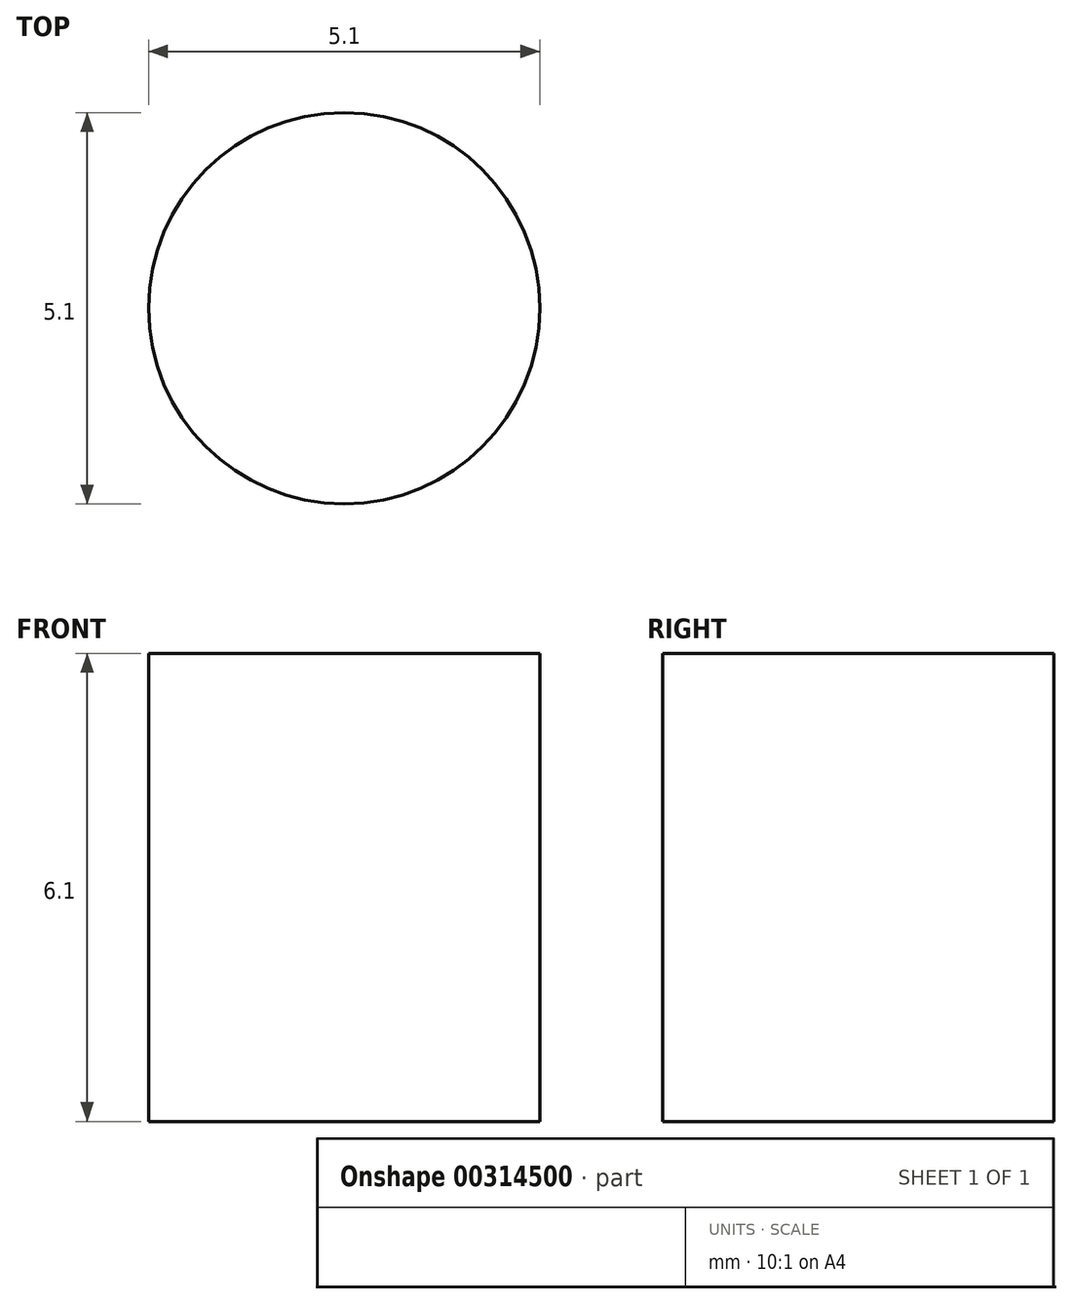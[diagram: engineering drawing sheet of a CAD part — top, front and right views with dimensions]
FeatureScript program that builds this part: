
annotation { "Feature Type Name" : "Feature", "Feature Type Description" : "" }
export const myFeature = defineFeature(function(context is Context, id is Id, definition is map)
    precondition{}
    {
        {
            var Q0;
            Q0=qCreatedBy(makeId("Top.planeOp"),FACE);
            var sketch = newSketch(context, id + "F0", { "sketchPlane" : qUnion([Q0])});
            skCircle(sketch, "E0", {"center": v(-26.5, 0) * mm, "radius": 2.55 * mm});
            skCircle(sketch, "E1", {"center": v(5.29, 10) * mm, "radius": 2.55 * mm});
            skCircle(sketch, "E2", {"center": v(5.29, 0) * mm, "radius": 2.55 * mm});
            skCircle(sketch, "E3", {"center": v(5.29, -10) * mm, "radius": 2.55 * mm});
            skCircle(sketch, "E4", {"center": v(25.29, -10) * mm, "radius": 2.55 * mm});
            skCircle(sketch, "E5", {"center": v(25.29, 0) * mm, "radius": 2.55 * mm});
            skCircle(sketch, "E6", {"center": v(25.29, 10) * mm, "radius": 2.55 * mm});
            skArc(sketch, "E7", {"start": v(-28.5, 19.75) * mm, "mid": v(-32.04, 18.29) * mm, "end": v(-33.5, 14.75) * mm});
            skLineSegment(sketch, "E8", {"start": v(-33.5, -14.75) * mm, "end": v(-33.5, 14.75) * mm});
            skArc(sketch, "E9", {"start": v(-33.5, -14.75) * mm, "mid": v(-32.04, -18.29) * mm, "end": v(-28.5, -19.75) * mm});
            skLineSegment(sketch, "E10", {"start": v(28.5, -19.75) * mm, "end": v(-28.5, -19.75) * mm});
            skArc(sketch, "E11", {"start": v(28.5, -19.75) * mm, "mid": v(32.04, -18.29) * mm, "end": v(33.5, -14.75) * mm});
            skLineSegment(sketch, "E12", {"start": v(33.5, 14.75) * mm, "end": v(33.5, -14.75) * mm});
            skLineSegment(sketch, "E13", {"start": v(28.5, 19.75) * mm, "end": v(-28.5, 19.75) * mm});
            skArc(sketch, "E14", {"start": v(33.5, 14.75) * mm, "mid": v(32.04, 18.29) * mm, "end": v(28.5, 19.75) * mm});
            skSolve(sketch);
        }
        {
            var Q0;
            Q0=makeQuery(id+"F0.imprint","IMPRINT",FACE,{"disambiguationData":[TD([[makeQuery(id+"F0.imprint","IMPRINT",EDGE,{"derivedFrom":sQuery(id+"F0.wireOp",EDGE,"E0")}),1.0]])]});
            extrude(context, id + "F1", {"entities" : qUnion([Q0]), "depth" : 6.1 * mm});
        }
    });
